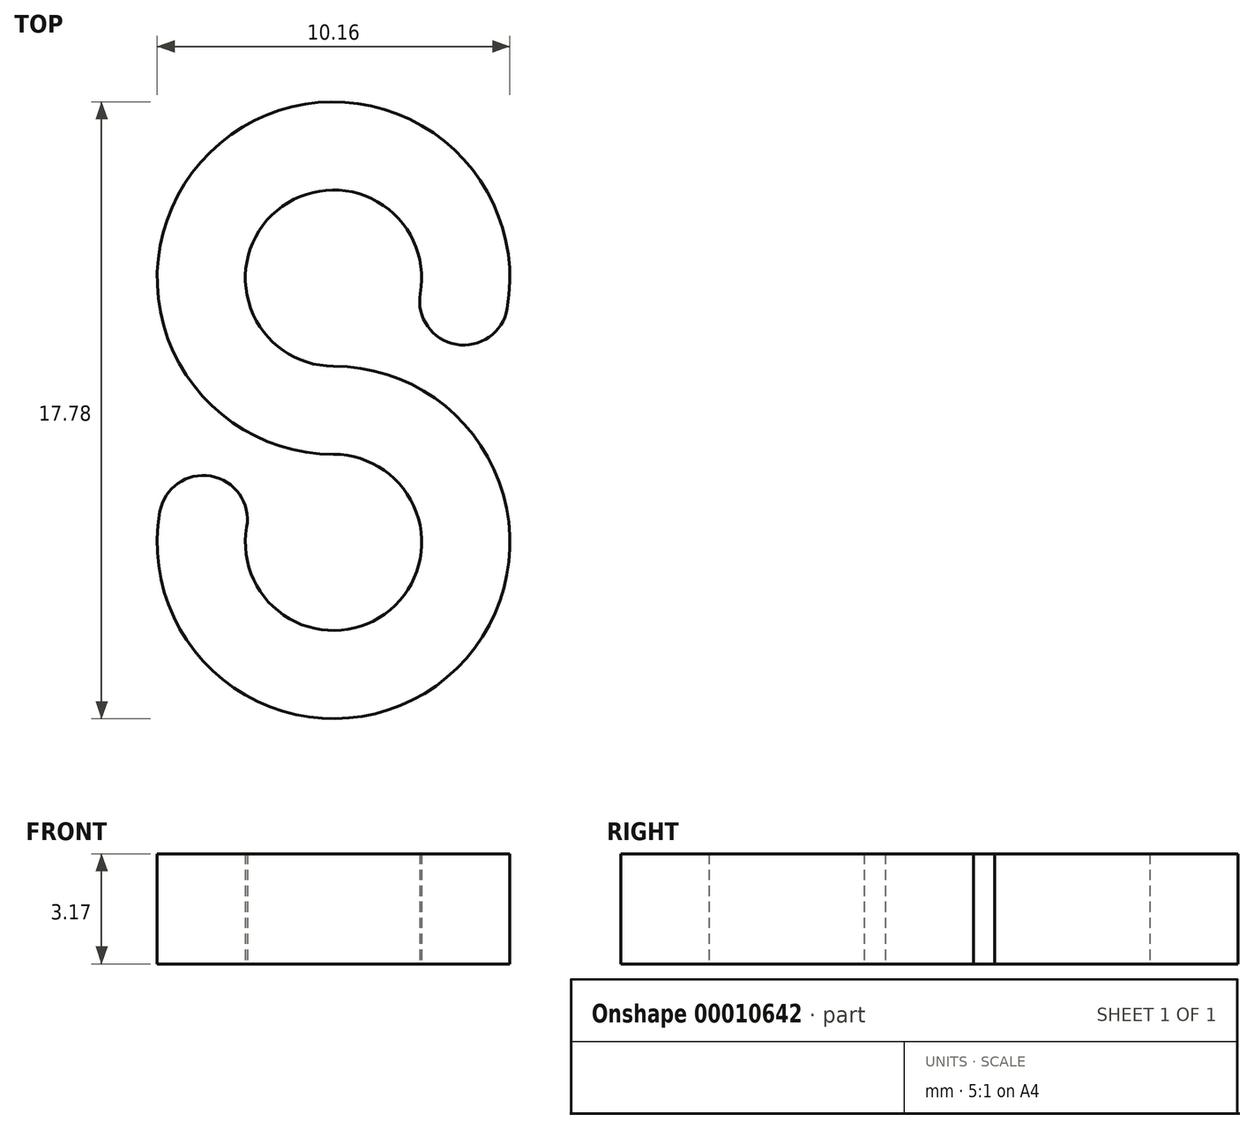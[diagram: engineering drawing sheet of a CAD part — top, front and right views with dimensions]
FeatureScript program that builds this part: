
annotation { "Feature Type Name" : "Feature", "Feature Type Description" : "" }
export const myFeature = defineFeature(function(context is Context, id is Id, definition is map)
    precondition{}
    {
        {
            var Q0;
            Q0=qCreatedBy(makeId("Top.planeOp"),FACE);
            var sketch = newSketch(context, id + "F0", { "sketchPlane" : qUnion([Q0])});
            skArc(sketch, "E0", {"start": v(3.75, 3.15) * mm, "mid": v(-2.45, 6.73) * mm, "end": v(0, 0) * mm, "construction": true});
            skLineSegment(sketch, "E1", {"start": v(0, 3.81) * mm, "end": v(3.75, 3.15) * mm, "construction": true});
            skLineSegment(sketch, "E2", {"start": v(0, 3.81) * mm, "end": v(3.81, 3.81) * mm, "construction": true});
            skArc(sketch, "E3.0", {"start": v(5, 2.93) * mm, "mid": v(-3.27, 7.7) * mm, "end": v(0, -1.27) * mm});
            skLineSegment(sketch, "E4", {"start": v(0, 3.81) * mm, "end": v(0, -1.27) * mm, "construction": true});
            skLineSegment(sketch, "E5", {"start": v(0, 3.81) * mm, "end": v(0, 0) * mm, "construction": true});
            skArc(sketch, "E6.0", {"start": v(2.5, 3.37) * mm, "mid": v(-1.63, 5.76) * mm, "end": v(0, 1.27) * mm});
            skArc(sketch, "E7", {"start": v(2.5, 3.37) * mm, "mid": v(3.53, 1.9) * mm, "end": v(5, 2.93) * mm});
            skArc(sketch, "E8", {"start": v(-3.75, -3.15) * mm, "mid": v(3.24, -5.82) * mm, "end": v(-2.26, -0.74) * mm, "construction": true});
            skLineSegment(sketch, "E9", {"start": v(0, -3.81) * mm, "end": v(-3.81, -3.81) * mm, "construction": true});
            skLineSegment(sketch, "E10", {"start": v(0, -3.81) * mm, "end": v(-3.75, -3.15) * mm, "construction": true});
            skArc(sketch, "E11", {"start": v(-5, -2.93) * mm, "mid": v(3.27, -7.7) * mm, "end": v(0, 1.27) * mm});
            skArc(sketch, "E12", {"start": v(-2.5, -3.37) * mm, "mid": v(1.63, -5.76) * mm, "end": v(0, -1.27) * mm});
            skArc(sketch, "E13", {"start": v(-2.5, -3.37) * mm, "mid": v(-3.53, -1.9) * mm, "end": v(-5, -2.93) * mm});
            skSolve(sketch);
        }
        {
            var Q0;
            Q0 = qSketchRegion(id + "F0", true);
            extrude(context, id + "F1", {"entities" : qUnion([Q0]), "depth" : 3.17 * mm});
        }
    });
